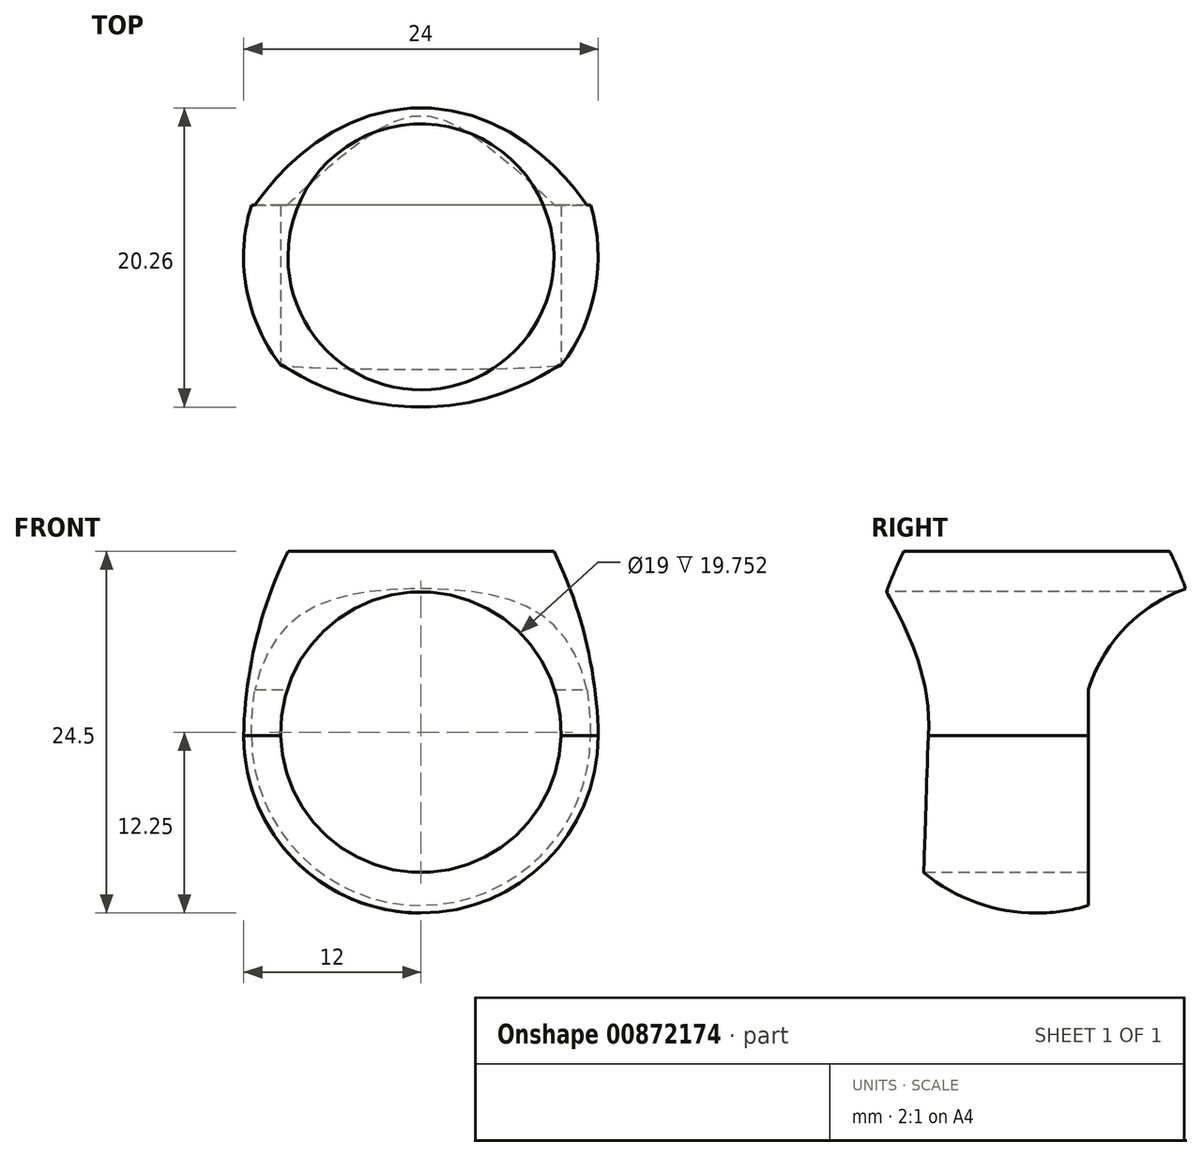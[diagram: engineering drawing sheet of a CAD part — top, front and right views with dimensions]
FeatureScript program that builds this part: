
annotation { "Feature Type Name" : "Feature", "Feature Type Description" : "" }
export const myFeature = defineFeature(function(context is Context, id is Id, definition is map)
    precondition{}
    {
        {
            var Q0;
            Q0=qCreatedBy(makeId("Front.planeOp"),FACE);
            var sketch = newSketch(context, id + "F0", { "sketchPlane" : qUnion([Q0])});
            skLineSegment(sketch, "E0", {"start": v(0, -24.5) * mm, "end": v(0, 0) * mm});
            skPoint(sketch, "E1.0", {"position": v(0, 0) * mm});
            skLineSegment(sketch, "E2", {"start": v(0, 0) * mm, "end": v(-9, 0) * mm});
            skPoint(sketch, "E3", {"position": v(0, -12.5) * mm});
            skLineSegment(sketch, "E4", {"start": v(0, -12.5) * mm, "end": v(-12, -12.5) * mm});
            skArc(sketch, "E5", {"start": v(-12, -12.5) * mm, "mid": v(-8.49, -20.99) * mm, "end": v(0, -24.5) * mm});
            skArc(sketch, "E6", {"start": v(-9, 0) * mm, "mid": v(-11.18, -6.09) * mm, "end": v(-12, -12.5) * mm});
            skSolve(sketch);
        }
        {
            var Q0;
            Q0=qSketchRegion(id+"F0",true);
            var Q1;
            Q1=sQuery(id+"F0.wireOp",EDGE,"E0");
            revolve(context, id + "F1", {"surfaceOperationType" : NewSurfaceOperationType.NEW, "entities" : qUnion([Q0]), "axis" : qUnion([Q1]), "revolveType" : RevolveType.FULL});
        }
        {
            var Q0;
            Q0=qCreatedBy(makeId("Front.planeOp"),FACE);
            var sketch = newSketch(context, id + "F2", { "sketchPlane" : qUnion([Q0])});
            skPoint(sketch, "E7", {"position": v(0, -12.25) * mm});
            skCircle(sketch, "E8", {"center": v(0, -12.25) * mm, "radius": 9.5 * mm});
            skSolve(sketch);
        }
        {
            var Q0;
            Q0=qSketchRegion(id+"F2",true);
            extrude(context, id + "F3", {"entities" : qUnion([Q0]), "operationType" : NewBodyOperationType.REMOVE, "endBound" : BoundingType.SYMMETRIC, "oppositeDirection" : true, "depth" : 25.4 * mm, "offsetDistance" : 25.4 * mm});
        }
        {
            var Q0;
            Q0=qCreatedBy(makeId("Right.planeOp"),FACE);
            var sketch = newSketch(context, id + "F4", { "sketchPlane" : qUnion([Q0])});
            skLineSegment(sketch, "E9", {"start": v(0, 0) * mm, "end": v(9, 0) * mm});
            skLineSegment(sketch, "E10", {"start": v(3.5, -26.5) * mm, "end": v(11.74, -26.5) * mm});
            skLineSegment(sketch, "E11", {"start": v(11.74, -2.5) * mm, "end": v(11.74, -26.5) * mm});
            skLineSegment(sketch, "E12", {"start": v(11.74, -2.5) * mm, "end": v(11.74, -12.5) * mm});
            skArc(sketch, "E13", {"start": v(10.25, -2.5) * mm, "mid": v(6.04, -5.13) * mm, "end": v(3.5, -9.39) * mm});
            skLineSegment(sketch, "E14", {"start": v(3.5, -26.5) * mm, "end": v(3.5, -9.39) * mm});
            skLineSegment(sketch, "E15", {"start": v(0, 0) * mm, "end": v(-9, 0) * mm});
            skPoint(sketch, "E16.endSnap0", {"position": v(-4.5, 0) * mm});
            skLineSegment(sketch, "E17", {"start": v(11.74, -2.5) * mm, "end": v(11.74, -2.14) * mm});
            skLineSegment(sketch, "E18", {"start": v(11.74, -2.14) * mm, "end": v(10.25, -2.5) * mm});
            skSolve(sketch);
        }
        {
            var Q0;
            Q0=makeQuery(id+"F4.imprint","IMPRINT",FACE,{"disambiguationData":[TD([[makeQuery(id+"F4.imprint","IMPRINT",EDGE,{"derivedFrom":sQuery(id+"F4.wireOp",EDGE,"E10")}),1.0]])]});
            extrude(context, id + "F5", {"entities" : qUnion([Q0]), "operationType" : NewBodyOperationType.REMOVE, "endBound" : BoundingType.SYMMETRIC, "oppositeDirection" : true, "depth" : 25.4 * mm, "offsetDistance" : 25.4 * mm});
        }
    });
